# Revit family: Deca_Sif+úo para Lavat+¦rio_1684.C.100.112
name_source: partatom
category: Conexões hidráulicas
revit_build: Autodesk Revit 2013 (Build: 20120221_2030(x64)
units: mm (PartAtom-declared; Revit-internal decimal feet)

## types (2) — shared parameters
Aprovado por = Contino/quattroD
Atendimento ao Cliente = 0800-0117073
Consumo = Varia com a pressão
Criado por = Contino/quattroD
Código de montagem = D2020
Descrição = Sifão para lavatório Slim 1 x 1 1/2
Diâmetro Ponto de Esgoto = 25  [stored 0.082021 ft]
Diâmetro Saída Esgoto = 40  [stored 0.131234 ft]
Fabricante = Deca
Flow Pressure = 0.00 psi
Informações Complementares = Não Aplicável
Linha = Sifão
Louça/Metais = Metal
Material = Latão Cromado e Plástico de Engenharia
Norma = ABNT NBR 14162:2011
Peso Liquido (Kg) = 1.236
Pressão = 2 A 40 mca
Produto = Sifão para lavatório Slim 1 x 1 1/2
Raio Ponto de Esgoto = 13
Raio Saída Esgoto = 20  [stored 0.0656168 ft]
Segmento = Luxo
URL = www.deca.com.br/produtos
Variações de COR = Cromado (1684.C.100.112); Dourado (1684.D.100.112)
Vendido Separadamente = Não Aplicável
zero-valued in all types: CWFU, Elevação-padrão, WFU

## per-type parameters (varying)
| type | Código | Modelo | Sifão |
| 1684.C.100.112_Cromado CR10 | 1684.C.100.112 | 1684.C.100.112 | Deca CR10 Cromado Metal |
| 1684.D.100.112_ Dourado | 1684.D.100.112 | 1684.D.100.112 | Deca GLD Gold Metal |

note: [stored X ft] marks values corroborated as IEEE doubles in the binary element streams (Revit-internal decimal feet)

## geometry (parser evidence)
native form markers: Blend x10, Sweep x1
no freeform markers — native parametric forms only
